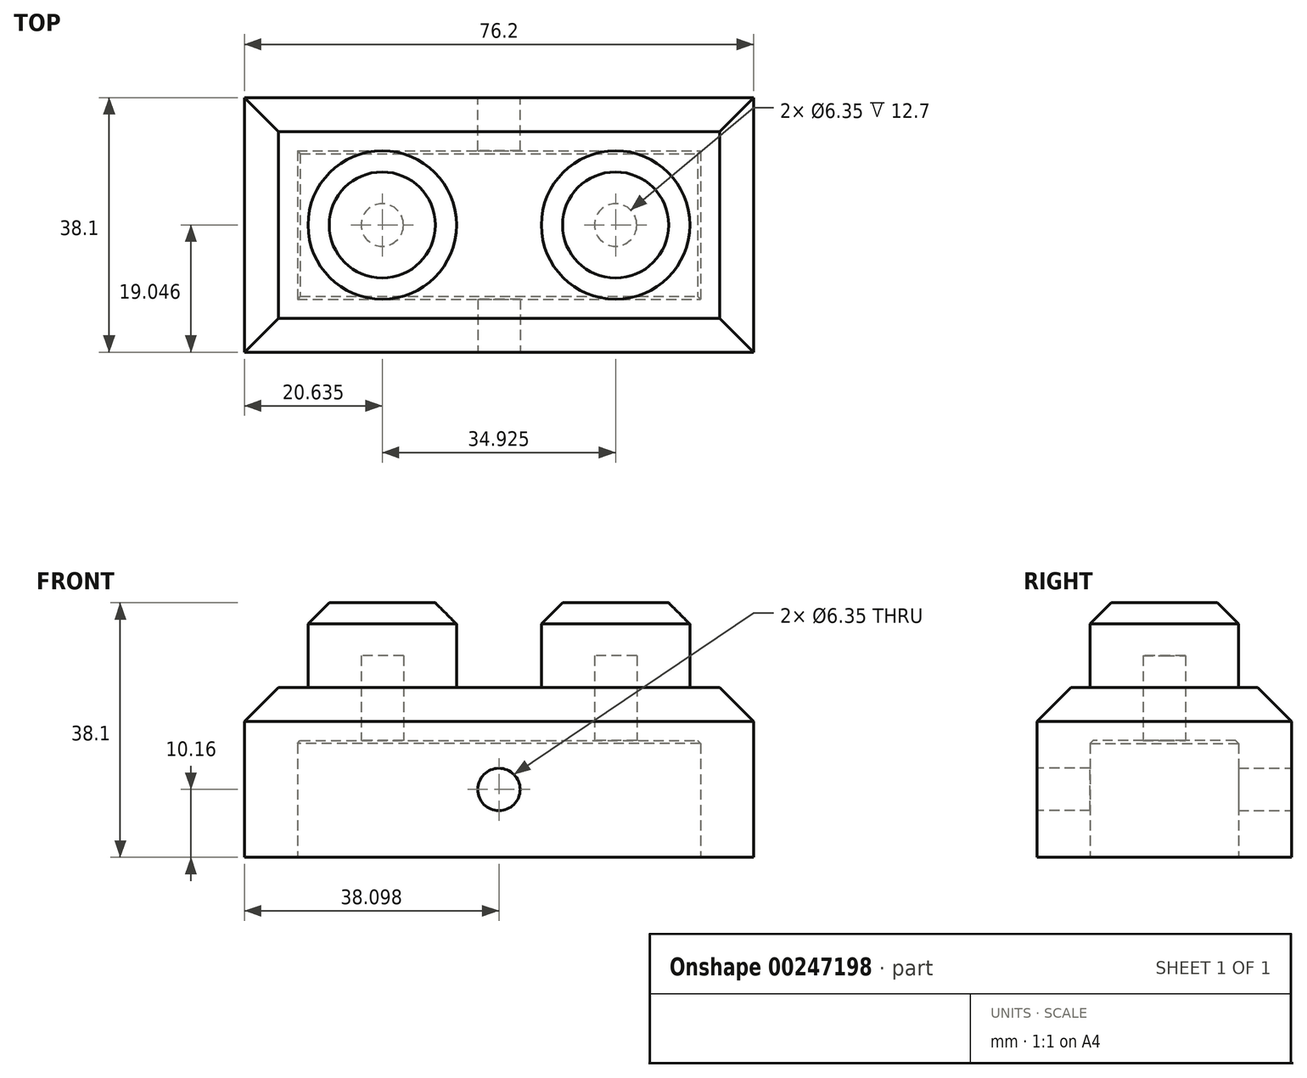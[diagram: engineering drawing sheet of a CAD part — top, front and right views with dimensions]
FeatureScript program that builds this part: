
annotation { "Feature Type Name" : "Feature", "Feature Type Description" : "" }
export const myFeature = defineFeature(function(context is Context, id is Id, definition is map)
    precondition{}
    {
        {
            var Q0;
            Q0=qCreatedBy(makeId("Top.planeOp"),FACE);
            var sketch = newSketch(context, id + "F0", { "sketchPlane" : qUnion([Q0])});
            skLineSegment(sketch, "E0.bottom", {"start": v(-50.82, 29.77) * mm, "end": v(25.38, 29.77) * mm});
            skLineSegment(sketch, "E0.top", {"start": v(-50.82, -8.33) * mm, "end": v(25.38, -8.33) * mm});
            skLineSegment(sketch, "E0.left", {"start": v(-50.82, 29.77) * mm, "end": v(-50.82, -8.33) * mm});
            skLineSegment(sketch, "E0.right", {"start": v(25.38, 29.77) * mm, "end": v(25.38, -8.33) * mm});
            skSolve(sketch);
        }
        {
            var Q0;
            Q0 = qSketchRegion(id + "F0", true);
            extrude(context, id + "F1", {"entities" : qUnion([Q0]), "depth" : 25.4 * mm});
        }
        {
            var Q0;
            Q0=makeQuery(id+"F1.opExtrude","CAP_EDGE",EDGE,{"disambiguationData":[OSD([sQuery(id+"F0.wireOp",EDGE,"E0.left")])],"isStart":false});
            var Q1;
            Q1=makeQuery(id+"F1.opExtrude","CAP_FACE",FACE,{"disambiguationData":[OSD([sQuery(id+"F0.wireOp",EDGE,"E0.bottom"),sQuery(id+"F0.wireOp",EDGE,"E0.top"),sQuery(id+"F0.wireOp",EDGE,"E0.left"),sQuery(id+"F0.wireOp",EDGE,"E0.right")])],"isStart":false});
            chamfer(context, id + "F2", {"entities" : qUnion([Q0, Q1]), "width" : 5.08 * mm, "tangentPropagation" : true});
        }
        {
            var Q0;
            Q0=makeQuery(id+"F1.opExtrude","CAP_FACE",FACE,{"disambiguationData":[OSD([sQuery(id+"F0.wireOp",EDGE,"E0.bottom"),sQuery(id+"F0.wireOp",EDGE,"E0.top"),sQuery(id+"F0.wireOp",EDGE,"E0.left"),sQuery(id+"F0.wireOp",EDGE,"E0.right")])],"isStart":false});
            var sketch = newSketch(context, id + "F3", { "sketchPlane" : qUnion([Q0])});
            skCircle(sketch, "E1", {"center": v(-30.18, 10.72) * mm, "radius": 11.11 * mm});
            skCircle(sketch, "E2", {"center": v(4.74, 10.72) * mm, "radius": 11.11 * mm});
            skSolve(sketch);
        }
        {
            var Q0;
            Q0 = qSketchRegion(id + "F3", true);
            extrude(context, id + "F4", {"entities" : qUnion([Q0]), "operationType" : NewBodyOperationType.ADD, "depth" : 12.7 * mm});
        }
        {
            var Q0;
            Q0=makeQuery(id+"F4.opExtrude","CAP_EDGE",EDGE,{"disambiguationData":[OSD([sQuery(id+"F3.wireOp",EDGE,"E1")])],"isStart":false});
            var Q1;
            Q1=makeQuery(id+"F4.opExtrude","CAP_EDGE",EDGE,{"disambiguationData":[OSD([sQuery(id+"F3.wireOp",EDGE,"E2")])],"isStart":false});
            chamfer(context, id + "F5", {"entities" : qUnion([Q0, Q1]), "width" : 3.17 * mm, "tangentPropagation" : true});
        }
        {
            var Q0;
            Q0=makeQuery(id+"F1.opExtrude","SWEPT_FACE",FACE,{"disambiguationData":[OSD([sQuery(id+"F0.wireOp",EDGE,"E0.top")])]});
            var sketch = newSketch(context, id + "F6", { "sketchPlane" : qUnion([Q0])});
            skCircle(sketch, "E3", {"center": v(-12.72, 10.16) * mm, "radius": 3.18 * mm});
            skSolve(sketch);
        }
        {
            var Q0;
            Q0=makeQuery(id+"F1.opExtrude","CAP_FACE",FACE,{"disambiguationData":[OSD([sQuery(id+"F0.wireOp",EDGE,"E0.bottom"),sQuery(id+"F0.wireOp",EDGE,"E0.top"),sQuery(id+"F0.wireOp",EDGE,"E0.left"),sQuery(id+"F0.wireOp",EDGE,"E0.right")])],"isStart":true});
            shell(context, id + "F7", {"entities" : qUnion([Q0]), "thickness" : 7.94 * mm});
        }
        {
            var Q0;
            Q0 = qSketchRegion(id + "F6", true);
            extrude(context, id + "F8", {"entities" : qUnion([Q0]), "operationType" : NewBodyOperationType.REMOVE, "oppositeDirection" : true, "depth" : 7.94 * mm});
        }
        {
            var Q0;
            Q0=makeQuery(id+"F1.opExtrude","SWEPT_FACE",FACE,{"disambiguationData":[OSD([sQuery(id+"F0.wireOp",EDGE,"E0.bottom")])]});
            var sketch = newSketch(context, id + "F9", { "sketchPlane" : qUnion([Q0])});
            skCircle(sketch, "E4", {"center": v(12.72, 10.16) * mm, "radius": 3.18 * mm});
            skPoint(sketch, "E4.centerSnap0", {"position": v(12.72, 0) * mm});
            skSolve(sketch);
        }
        {
            var Q0;
            Q0 = qSketchRegion(id + "F9", true);
            extrude(context, id + "F10", {"entities" : qUnion([Q0]), "operationType" : NewBodyOperationType.REMOVE, "oppositeDirection" : true, "depth" : 7.94 * mm});
        }
    });
